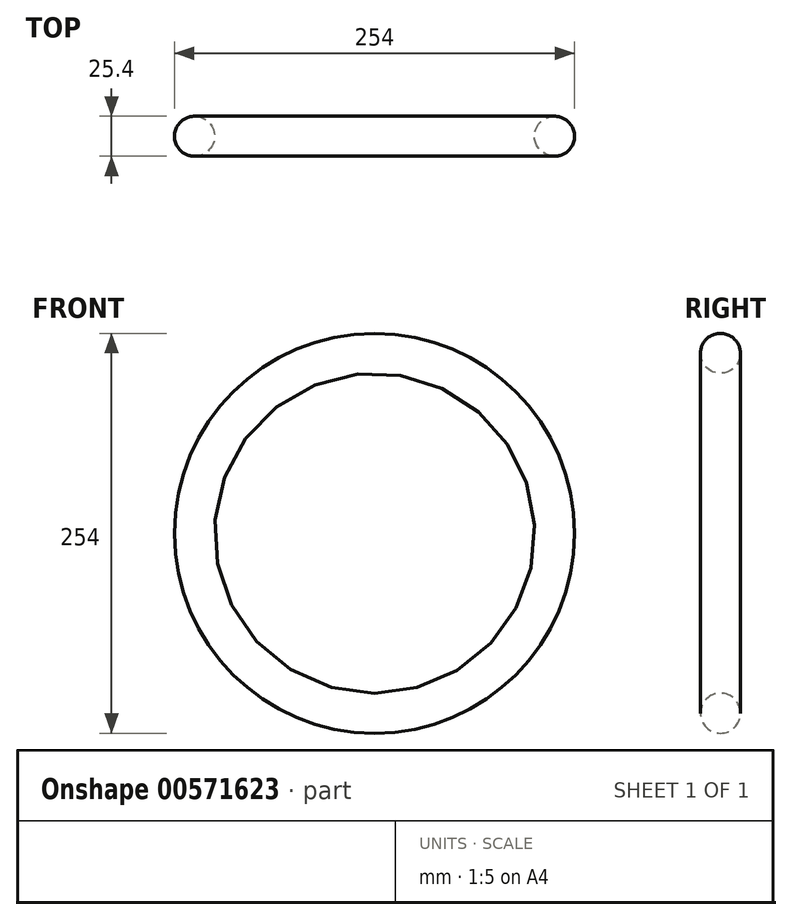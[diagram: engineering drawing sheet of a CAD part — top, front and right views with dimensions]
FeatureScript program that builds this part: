
annotation { "Feature Type Name" : "Feature", "Feature Type Description" : "" }
export const myFeature = defineFeature(function(context is Context, id is Id, definition is map)
    precondition{}
    {
        {
            var Q0;
            Q0=qCreatedBy(makeId("Top.planeOp"),FACE);
            var sketch = newSketch(context, id + "F0", { "sketchPlane" : qUnion([Q0])});
            skCircle(sketch, "E0", {"center": v(114.3, 0) * mm, "radius": 12.7 * mm});
            skLineSegment(sketch, "E1", {"start": v(0, 0) * mm, "end": v(0, 36.84) * mm});
            skSolve(sketch);
        }
        {
            var Q0;
            Q0=makeQuery(id+"F0.imprint","IMPRINT",FACE,{"disambiguationData":[TD([[makeQuery(id+"F0.imprint","IMPRINT",EDGE,{"derivedFrom":sQuery(id+"F0.wireOp",EDGE,"E0")}),1.0]])]});
            var Q1;
            Q1=sQuery(id+"F0.wireOp",EDGE,"E1");
            revolve(context, id + "F1", {"entities" : qUnion([Q0]), "axis" : qUnion([Q1]), "revolveType" : RevolveType.FULL});
        }
    });
